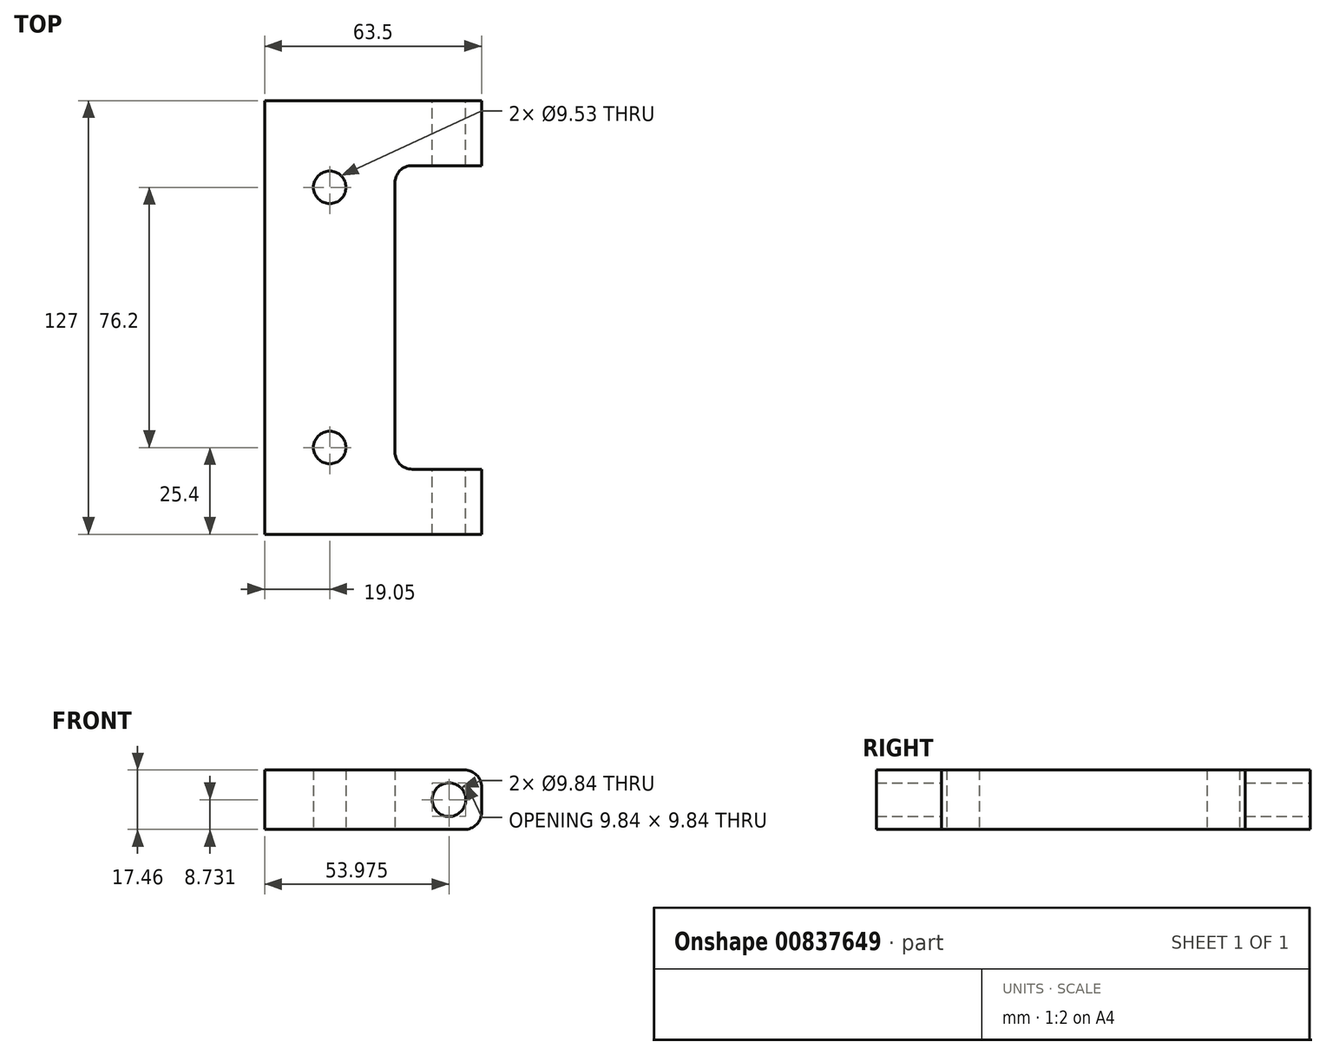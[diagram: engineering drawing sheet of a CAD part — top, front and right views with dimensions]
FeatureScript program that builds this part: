
annotation { "Feature Type Name" : "Feature", "Feature Type Description" : "" }
export const myFeature = defineFeature(function(context is Context, id is Id, definition is map)
    precondition{}
    {
        {
            var Q0;
            Q0=qCreatedBy(makeId("Top.planeOp"),FACE);
            var sketch = newSketch(context, id + "F0", { "sketchPlane" : qUnion([Q0])});
            skLineSegment(sketch, "E0.bottom", {"start": v(31.75, -63.5) * mm, "end": v(-31.75, -63.5) * mm});
            skLineSegment(sketch, "E0.top", {"start": v(31.75, 63.5) * mm, "end": v(-31.75, 63.5) * mm});
            skLineSegment(sketch, "E0.left", {"start": v(31.75, -63.5) * mm, "end": v(31.75, -44.45) * mm});
            skLineSegment(sketch, "E0.right", {"start": v(-31.75, -63.5) * mm, "end": v(-31.75, 63.5) * mm});
            skPoint(sketch, "E0.middle", {"position": v(0, 0) * mm});
            skLineSegment(sketch, "E1", {"start": v(31.75, 44.45) * mm, "end": v(6.35, 44.45) * mm});
            skLineSegment(sketch, "E2", {"start": v(6.35, 44.45) * mm, "end": v(6.35, -44.45) * mm});
            skLineSegment(sketch, "E3", {"start": v(6.35, -44.45) * mm, "end": v(31.75, -44.45) * mm});
            skLineSegment(sketch, "E4.trimOffspring", {"start": v(31.75, 44.45) * mm, "end": v(31.75, 63.5) * mm});
            skSolve(sketch);
        }
        {
            var Q0;
            Q0 = qSketchRegion(id + "F0", true);
            extrude(context, id + "F1", {"entities" : qUnion([Q0]), "depth" : 17.46 * mm, "offsetDistance" : 25.4 * mm});
        }
        {
            var Q0;
            Q0=makeQuery(id+"F1.opExtrude","SWEPT_FACE",FACE,{"disambiguationData":[OSD([sQuery(id+"F0.wireOp",EDGE,"E0.top")])]});
            var sketch = newSketch(context, id + "F2", { "sketchPlane" : qUnion([Q0])});
            skPoint(sketch, "E5", {"position": v(-22.22, 8.73) * mm});
            skSolve(sketch);
        }
        {
            var Q0;
            Q0=sQuery(id+"F2.wireOp",VERTEX,"E5");
            var Q1;
            Q1=makeQuery(id+"F1.opExtrude","SWEPT_BODY",BODY,{"disambiguationData":[OSD([sQuery(id+"F0.wireOp",EDGE,"E0.bottom"),sQuery(id+"F0.wireOp",EDGE,"E0.top"),sQuery(id+"F0.wireOp",EDGE,"E0.left"),sQuery(id+"F0.wireOp",EDGE,"E0.right"),sQuery(id+"F0.wireOp",EDGE,"E1"),sQuery(id+"F0.wireOp",EDGE,"E2"),sQuery(id+"F0.wireOp",EDGE,"E3"),sQuery(id+"F0.wireOp",EDGE,"E4.trimOffspring")])]});
            hole(context, id + "F3", {"style" : HoleStyle.SIMPLE, "endStyle" : HoleEndStyle.THROUGH, "holeDiameter" : 9.84 * mm, "majorDiameter" : 6.35 * mm, "isTappedThrough" : true, "tappedDepth" : 12.7 * mm, "tapClearance" : 3, "locations" : qUnion([Q0]), "scope" : qUnion([Q1])});
        }
        {
            var Q0;
            Q0=makeQuery(id+"F1.opExtrude","SWEPT_EDGE",EDGE,{"disambiguationData":[OSD([sQuery(id+"F0.wireOp",EDGE,"E2"),sQuery(id+"F0.wireOp",EDGE,"E3")])]});
            var Q1;
            Q1=makeQuery(id+"F1.opExtrude","SWEPT_EDGE",EDGE,{"disambiguationData":[OSD([sQuery(id+"F0.wireOp",EDGE,"E1"),sQuery(id+"F0.wireOp",EDGE,"E2")])]});
            fillet(context, id + "F4", {"entities" : qUnion([Q0, Q1]), "radius" : 5.08 * mm, "tangentPropagation" : true, "allowEdgeOverflow" : false});
        }
        {
            var Q0;
            Q0=makeQuery(id+"F1.opExtrude","CAP_FACE",FACE,{"disambiguationData":[OSD([sQuery(id+"F0.wireOp",EDGE,"E0.bottom"),sQuery(id+"F0.wireOp",EDGE,"E0.top"),sQuery(id+"F0.wireOp",EDGE,"E0.left"),sQuery(id+"F0.wireOp",EDGE,"E0.right"),sQuery(id+"F0.wireOp",EDGE,"E1"),sQuery(id+"F0.wireOp",EDGE,"E2"),sQuery(id+"F0.wireOp",EDGE,"E3"),sQuery(id+"F0.wireOp",EDGE,"E4.trimOffspring")])],"isStart":true});
            var sketch = newSketch(context, id + "F5", { "sketchPlane" : qUnion([Q0])});
            skPoint(sketch, "E6", {"position": v(-12.7, 38.1) * mm});
            skPoint(sketch, "E7", {"position": v(-12.7, -38.1) * mm});
            skSolve(sketch);
        }
        {
            var Q0;
            Q0=sQuery(id+"F5.wireOp",VERTEX,"E6");
            var Q1;
            Q1=sQuery(id+"F5.wireOp",VERTEX,"E7");
            var Q2;
            Q2=makeQuery(id+"F1.opExtrude","SWEPT_BODY",BODY,{"disambiguationData":[OSD([sQuery(id+"F0.wireOp",EDGE,"E0.bottom"),sQuery(id+"F0.wireOp",EDGE,"E0.top"),sQuery(id+"F0.wireOp",EDGE,"E0.left"),sQuery(id+"F0.wireOp",EDGE,"E0.right"),sQuery(id+"F0.wireOp",EDGE,"E1"),sQuery(id+"F0.wireOp",EDGE,"E2"),sQuery(id+"F0.wireOp",EDGE,"E3"),sQuery(id+"F0.wireOp",EDGE,"E4.trimOffspring")])]});
            hole(context, id + "F6", {"style" : HoleStyle.SIMPLE, "endStyle" : HoleEndStyle.THROUGH, "holeDiameter" : 9.52 * mm, "majorDiameter" : 6.35 * mm, "isTappedThrough" : true, "tappedDepth" : 12.7 * mm, "tapClearance" : 3, "locations" : qUnion([Q0, Q1]), "scope" : qUnion([Q2])});
        }
        {
            var Q0;
            Q0=makeQuery(id+"F1.opExtrude","CAP_EDGE",EDGE,{"disambiguationData":[OSD([sQuery(id+"F0.wireOp",EDGE,"E0.left")])],"isStart":false});
            var Q1;
            Q1=makeQuery(id+"F1.opExtrude","CAP_EDGE",EDGE,{"disambiguationData":[OSD([sQuery(id+"F0.wireOp",EDGE,"E0.left")])],"isStart":true});
            var Q2;
            Q2=makeQuery(id+"F1.opExtrude","CAP_EDGE",EDGE,{"disambiguationData":[OSD([sQuery(id+"F0.wireOp",EDGE,"E4.trimOffspring")])],"isStart":false});
            var Q3;
            Q3=makeQuery(id+"F1.opExtrude","CAP_EDGE",EDGE,{"disambiguationData":[OSD([sQuery(id+"F0.wireOp",EDGE,"E4.trimOffspring")])],"isStart":true});
            fillet(context, id + "F7", {"entities" : qUnion([Q0, Q1, Q2, Q3]), "radius" : 5.08 * mm, "tangentPropagation" : true, "allowEdgeOverflow" : false});
        }
    });
